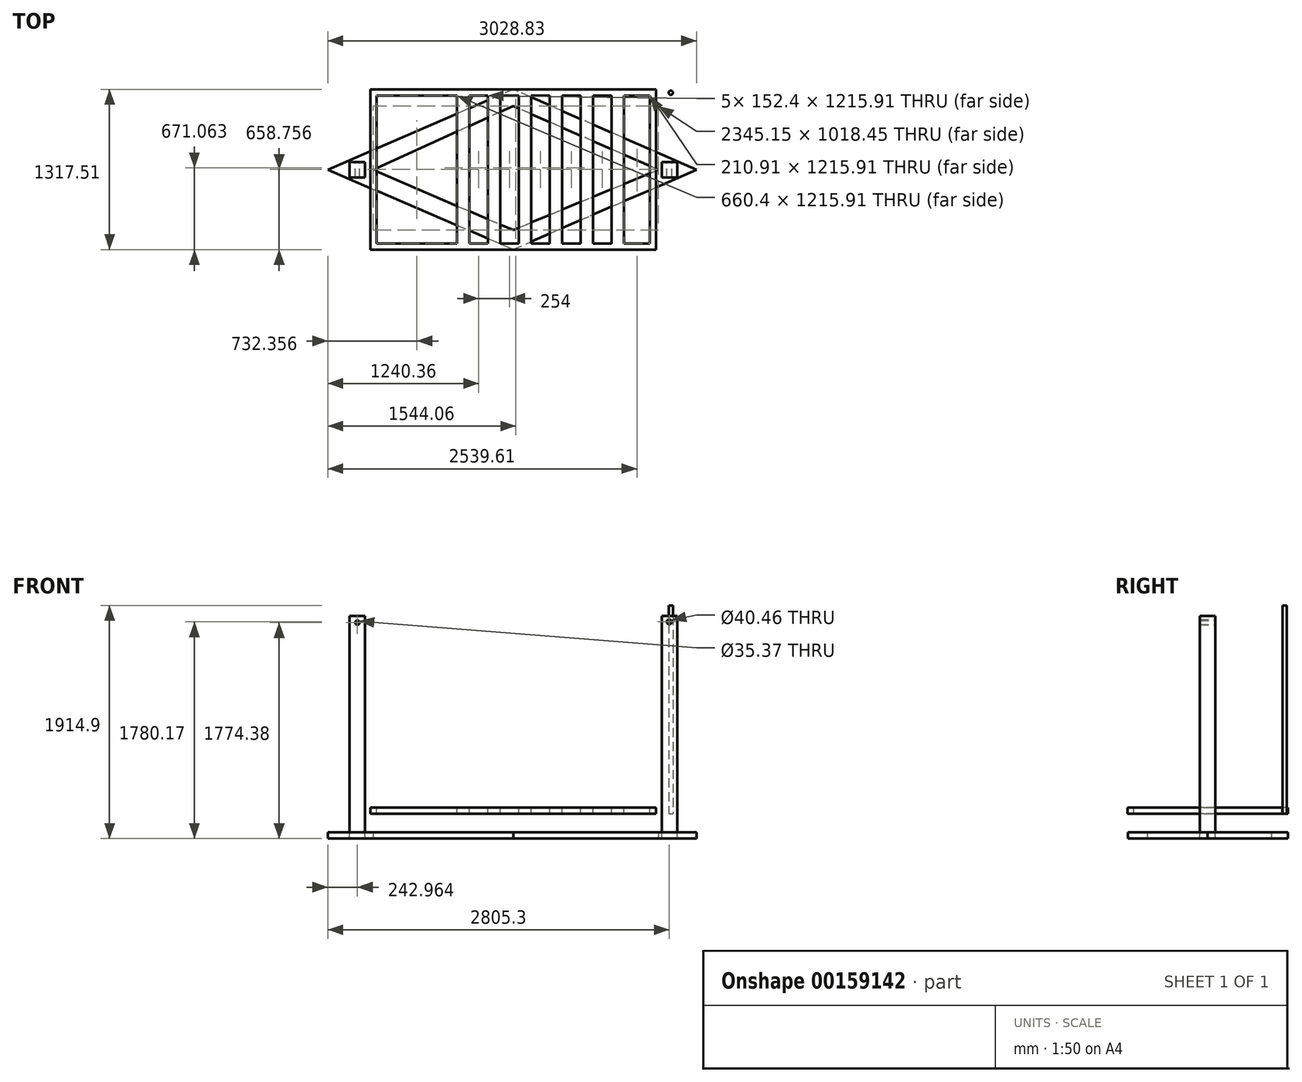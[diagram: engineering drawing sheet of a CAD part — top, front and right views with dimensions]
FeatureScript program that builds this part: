
annotation { "Feature Type Name" : "Feature", "Feature Type Description" : "" }
export const myFeature = defineFeature(function(context is Context, id is Id, definition is map)
    precondition{}
    {
        {
            var Q0;
            Q0=qCreatedBy(makeId("Front.planeOp"),FACE);
            var sketch = newSketch(context, id + "F0", { "sketchPlane" : qUnion([Q0])});
            skLineSegment(sketch, "E0", {"start": v(0, 0) * mm, "end": v(-1219.2, 0) * mm});
            skLineSegment(sketch, "E1", {"start": v(0, 0) * mm, "end": v(1219.2, 0) * mm});
            skLineSegment(sketch, "E2.bottom", {"start": v(-1219.2, 0) * mm, "end": v(-1346.2, 0) * mm});
            skLineSegment(sketch, "E2.top", {"start": v(-1219.2, 1828.8) * mm, "end": v(-1346.2, 1828.8) * mm});
            skLineSegment(sketch, "E2.left", {"start": v(-1219.2, 0) * mm, "end": v(-1219.2, 1828.8) * mm});
            skLineSegment(sketch, "E2.right", {"start": v(-1346.2, 0) * mm, "end": v(-1346.2, 1828.8) * mm});
            skLineSegment(sketch, "E3.bottom", {"start": v(1219.2, 0) * mm, "end": v(1346.2, 0) * mm});
            skLineSegment(sketch, "E3.top", {"start": v(1219.2, 1828.8) * mm, "end": v(1346.2, 1828.8) * mm});
            skLineSegment(sketch, "E3.left", {"start": v(1219.2, 0) * mm, "end": v(1219.2, 1828.8) * mm});
            skLineSegment(sketch, "E3.right", {"start": v(1346.2, 0) * mm, "end": v(1346.2, 1828.8) * mm});
            skSolve(sketch);
        }
        {
            var Q0;
            Q0=makeQuery(id+"F0.imprint","IMPRINT",FACE,{"disambiguationData":[TD([[makeQuery(id+"F0.imprint","IMPRINT",EDGE,{"derivedFrom":sQuery(id+"F0.wireOp",EDGE,"E2.bottom")}),-1.0]])]});
            var Q1;
            Q1=makeQuery(id+"F0.imprint","IMPRINT",FACE,{"disambiguationData":[TD([[makeQuery(id+"F0.imprint","IMPRINT",EDGE,{"derivedFrom":sQuery(id+"F0.wireOp",EDGE,"E3.bottom")}),1.0]])]});
            extrude(context, id + "F1", {"entities" : qUnion([Q0, Q1]), "depth" : 127 * mm, "symmetric" : true});
        }
        {
            var Q0;
            Q0=qCreatedBy(makeId("Top.planeOp"),FACE);
            var sketch = newSketch(context, id + "F2", { "sketchPlane" : qUnion([Q0])});
            skLineSegment(sketch, "E4.bottom", {"start": v(-1172.25, -656.01) * mm, "end": v(1172.25, -656.01) * mm});
            skLineSegment(sketch, "E4.top", {"start": v(-1172.25, 656.01) * mm, "end": v(1172.25, 656.01) * mm});
            skLineSegment(sketch, "E4.left", {"start": v(-1172.25, -656.01) * mm, "end": v(-1172.25, 656.01) * mm});
            skLineSegment(sketch, "E4.right", {"start": v(1172.25, -656.01) * mm, "end": v(1172.25, 656.01) * mm});
            skPoint(sketch, "E4.middle", {"position": v(0, 0) * mm});
            skSolve(sketch);
        }
        {
            var Q0;
            Q0 = qSketchRegion(id + "F2", true);
            extrude(context, id + "F3", {"entities" : qUnion([Q0]), "depth" : 76.2 * mm});
        }
        {
            var Q0;
            Q0=qCreatedBy(makeId("Front.planeOp"),FACE);
            var sketch = newSketch(context, id + "F4", { "sketchPlane" : qUnion([Q0])});
            skCircle(sketch, "E5", {"center": v(-1280.65, 1774.38) * mm, "radius": 17.68 * mm});
            skSolve(sketch);
        }
        {
            var Q0;
            Q0=makeQuery(id+"F4.imprint","IMPRINT",FACE,{"disambiguationData":[TD([[makeQuery(id+"F4.imprint","IMPRINT",EDGE,{"derivedFrom":sQuery(id+"F4.wireOp",EDGE,"E5")}),1.0]])]});
            extrude(context, id + "F5", {"entities" : qUnion([Q0]), "operationType" : NewBodyOperationType.REMOVE, "endBound" : BoundingType.THROUGH_ALL, "depth" : 147.7 * mm, "hasSecondDirection" : true, "secondDirectionOppositeDirection" : true, "secondDirectionDepth" : 166.4 * mm});
        }
        {
            var Q0;
            Q0=qCreatedBy(makeId("Front.planeOp"),FACE);
            var sketch = newSketch(context, id + "F6", { "sketchPlane" : qUnion([Q0])});
            skCircle(sketch, "E6", {"center": v(1281.68, 1780.17) * mm, "radius": 20.23 * mm});
            skSolve(sketch);
        }
        {
            var Q0;
            Q0 = qSketchRegion(id + "F6", true);
            extrude(context, id + "F7", {"entities" : qUnion([Q0]), "operationType" : NewBodyOperationType.REMOVE, "endBound" : BoundingType.UP_TO_NEXT, "depth" : 25.4 * mm, "hasSecondDirection" : true, "secondDirectionOppositeDirection" : true, "secondDirectionDepth" : 170.98 * mm});
        }
        {
            var Q0;
            Q0=qCreatedBy(makeId("Top.planeOp"),FACE);
            var sketch = newSketch(context, id + "F8", { "sketchPlane" : qUnion([Q0])});
            skLineSegment(sketch, "E7", {"start": v(-1523.6, 0) * mm, "end": v(0, -653.51) * mm});
            skLineSegment(sketch, "E8", {"start": v(0, -653.51) * mm, "end": v(1505.22, 0) * mm});
            skLineSegment(sketch, "E9", {"start": v(1505.22, 0) * mm, "end": v(0, 661.47) * mm});
            skLineSegment(sketch, "E10", {"start": v(0, 661.47) * mm, "end": v(-1523.6, 0) * mm});
            skLineSegment(sketch, "E11", {"start": v(-1152.12, 0) * mm, "end": v(0, -494.17) * mm});
            skLineSegment(sketch, "E12", {"start": v(0, -494.17) * mm, "end": v(1193.02, 0) * mm});
            skLineSegment(sketch, "E13", {"start": v(1193.02, 0) * mm, "end": v(0, 524.28) * mm});
            skLineSegment(sketch, "E14", {"start": v(0, 524.28) * mm, "end": v(-1152.12, 0) * mm});
            skSolve(sketch);
        }
        {
            var Q0;
            Q0=makeQuery(id+"F8.imprint","IMPRINT",FACE,{"disambiguationData":[TD([[makeQuery(id+"F8.imprint","IMPRINT",EDGE,{"derivedFrom":sQuery(id+"F8.wireOp",EDGE,"E7")}),1.0]])]});
            extrude(context, id + "F9", {"entities" : qUnion([Q0]), "depth" : 50.8 * mm});
        }
        {
            var Q0;
            Q0=makeQuery(id+"F3.opExtrude","SWEPT_FACE",FACE,{"disambiguationData":[OSD([sQuery(id+"F2.wireOp",EDGE,"E4.bottom")])]});
            var sketch = newSketch(context, id + "F10", { "sketchPlane" : qUnion([Q0])});
            skLineSegment(sketch, "E15.bottom", {"start": v(-1172.25, 389.27) * mm, "end": v(1172.25, 389.27) * mm});
            skLineSegment(sketch, "E15.top", {"start": v(-1172.25, 254) * mm, "end": v(1172.25, 254) * mm});
            skLineSegment(sketch, "E15.left", {"start": v(-1172.25, 389.27) * mm, "end": v(-1172.25, 254) * mm});
            skLineSegment(sketch, "E15.right", {"start": v(1172.25, 389.27) * mm, "end": v(1172.25, 254) * mm});
            skSolve(sketch);
        }
        {
            var Q0;
            Q0=makeQuery(id+"F10.imprint","IMPRINT",FACE,{"disambiguationData":[TD([[makeQuery(id+"F10.imprint","IMPRINT",EDGE,{"derivedFrom":sQuery(id+"F10.wireOp",EDGE,"E15.bottom")}),-1.0]])]});
            extrude(context, id + "F11", {"entities" : qUnion([Q0]), "oppositeDirection" : true, "depth" : 1320.8 * mm});
        }
        {
            var Q0;
            Q0=makeQuery(id+"F3.opExtrude","SWEPT_BODY",BODY,{"disambiguationData":[OSD([sQuery(id+"F2.wireOp",EDGE,"E4.bottom"),sQuery(id+"F2.wireOp",EDGE,"E4.top"),sQuery(id+"F2.wireOp",EDGE,"E4.left"),sQuery(id+"F2.wireOp",EDGE,"E4.right")])]});
            deleteBodies(context, id + "F12", {"entities" : qUnion([Q0])});
        }
        {
            var Q0;
            Q0=makeQuery(id+"F11.opExtrude","SWEPT_FACE",FACE,{"disambiguationData":[OSD([sQuery(id+"F10.wireOp",EDGE,"E15.top")])]});
            var sketch = newSketch(context, id + "F13", { "sketchPlane" : qUnion([Q0])});
            skLineSegment(sketch, "E16.bottom", {"start": v(-1172.25, 656.01) * mm, "end": v(1172.25, 656.01) * mm});
            skLineSegment(sketch, "E16.top", {"start": v(-1172.25, -661.5) * mm, "end": v(1172.25, -661.5) * mm});
            skLineSegment(sketch, "E16.left", {"start": v(-1172.25, 656.01) * mm, "end": v(-1172.25, -661.5) * mm});
            skLineSegment(sketch, "E16.right", {"start": v(1172.25, 656.01) * mm, "end": v(1172.25, -661.5) * mm});
            skLineSegment(sketch, "E17.0", {"start": v(-1121.45, 605.21) * mm, "end": v(1121.45, 605.21) * mm});
            skLineSegment(sketch, "E17.1", {"start": v(-1121.45, 605.21) * mm, "end": v(-1121.45, -610.7) * mm});
            skLineSegment(sketch, "E17.2", {"start": v(-1121.45, -610.7) * mm, "end": v(1121.45, -610.7) * mm});
            skLineSegment(sketch, "E17.3", {"start": v(1121.45, 605.21) * mm, "end": v(1121.45, -610.7) * mm});
            skLineSegment(sketch, "E18.bottom", {"start": v(-969.05, 605.21) * mm, "end": v(-867.45, 605.21) * mm});
            skLineSegment(sketch, "E18.top", {"start": v(-969.05, -610.7) * mm, "end": v(-867.45, -610.7) * mm});
            skLineSegment(sketch, "E18.left", {"start": v(-969.05, 605.21) * mm, "end": v(-969.05, -610.7) * mm});
            skLineSegment(sketch, "E18.right", {"start": v(-867.45, 605.21) * mm, "end": v(-867.45, -610.7) * mm});
            skLineSegment(sketch, "E19.bottom", {"start": v(-715.05, 605.21) * mm, "end": v(-613.45, 605.21) * mm});
            skLineSegment(sketch, "E19.top", {"start": v(-715.05, -610.7) * mm, "end": v(-613.45, -610.7) * mm});
            skLineSegment(sketch, "E19.left", {"start": v(-715.05, 605.21) * mm, "end": v(-715.05, -610.7) * mm});
            skLineSegment(sketch, "E19.right", {"start": v(-613.45, 605.21) * mm, "end": v(-613.45, -610.7) * mm});
            skLineSegment(sketch, "E20", {"start": v(-461.05, 605.21) * mm, "end": v(-461.05, -610.7) * mm});
            skLineSegment(sketch, "E21", {"start": v(-359.45, 605.21) * mm, "end": v(-359.45, -610.7) * mm});
            skLineSegment(sketch, "E22", {"start": v(-207.05, 605.21) * mm, "end": v(-207.05, -610.7) * mm});
            skPoint(sketch, "E22.endSnap0", {"position": v(0, -610.7) * mm});
            skLineSegment(sketch, "E23", {"start": v(-105.45, 605.21) * mm, "end": v(-105.45, -610.7) * mm});
            skLineSegment(sketch, "E24", {"start": v(46.95, 605.21) * mm, "end": v(46.95, -610.7) * mm});
            skLineSegment(sketch, "E25", {"start": v(148.55, 605.21) * mm, "end": v(148.55, -610.7) * mm});
            skLineSegment(sketch, "E26", {"start": v(300.95, 605.21) * mm, "end": v(300.95, -610.7) * mm});
            skLineSegment(sketch, "E27", {"start": v(402.55, 605.21) * mm, "end": v(402.55, -610.7) * mm});
            skLineSegment(sketch, "E28", {"start": v(554.95, 605.21) * mm, "end": v(554.95, -610.7) * mm});
            skLineSegment(sketch, "E29", {"start": v(656.55, 605.21) * mm, "end": v(656.55, -610.7) * mm});
            skLineSegment(sketch, "E30", {"start": v(808.95, 605.21) * mm, "end": v(808.95, -610.7) * mm});
            skLineSegment(sketch, "E31", {"start": v(910.55, 605.21) * mm, "end": v(910.55, -610.7) * mm});
            skSolve(sketch);
        }
        {
            var Q0;
            Q0=makeQuery(id+"F13.imprint","IMPRINT",FACE,{"disambiguationData":[TD([[makeQuery(id+"F13.imprint","IMPRINT",EDGE,{"derivedFrom":sQuery(id+"F13.wireOp",EDGE,"E16.bottom")}),-1.0]])]});
            var Q1;
            {var subQ0=sQuery(id+"F13.wireOp",EDGE,"E28");Q1=makeQuery(id+"F13.imprint","IMPRINT",FACE,{"disambiguationData":[TD([[makeQuery(id+"F13.imprint","IMPRINT",EDGE,{"derivedFrom":subQ0}),1.0]])]});}
            var Q2;
            {var subQ0=sQuery(id+"F13.wireOp",EDGE,"E22");Q2=makeQuery(id+"F13.imprint","IMPRINT",FACE,{"disambiguationData":[TD([[makeQuery(id+"F13.imprint","IMPRINT",EDGE,{"derivedFrom":subQ0}),1.0]])]});}
            var Q3;
            Q3=makeQuery(id+"F13.imprint","IMPRINT",FACE,{"disambiguationData":[TD([[makeQuery(id+"F13.imprint","IMPRINT",EDGE,{"derivedFrom":sQuery(id+"F13.wireOp",EDGE,"E19.bottom")}),-1.0]])]});
            var Q4;
            {var subQ0=sQuery(id+"F13.wireOp",EDGE,"E24");Q4=makeQuery(id+"F13.imprint","IMPRINT",FACE,{"disambiguationData":[TD([[makeQuery(id+"F13.imprint","IMPRINT",EDGE,{"derivedFrom":subQ0}),1.0]])]});}
            var Q5;
            {var subQ0=sQuery(id+"F13.wireOp",EDGE,"E20");Q5=makeQuery(id+"F13.imprint","IMPRINT",FACE,{"disambiguationData":[TD([[makeQuery(id+"F13.imprint","IMPRINT",EDGE,{"derivedFrom":subQ0}),1.0]])]});}
            var Q6;
            {var subQ0=sQuery(id+"F13.wireOp",EDGE,"E30");Q6=makeQuery(id+"F13.imprint","IMPRINT",FACE,{"disambiguationData":[TD([[makeQuery(id+"F13.imprint","IMPRINT",EDGE,{"derivedFrom":subQ0}),1.0]])]});}
            var Q7;
            Q7=makeQuery(id+"F13.imprint","IMPRINT",FACE,{"disambiguationData":[TD([[makeQuery(id+"F13.imprint","IMPRINT",EDGE,{"derivedFrom":sQuery(id+"F13.wireOp",EDGE,"E18.bottom")}),-1.0]])]});
            var Q8;
            {var subQ0=sQuery(id+"F13.wireOp",EDGE,"E26");Q8=makeQuery(id+"F13.imprint","IMPRINT",FACE,{"disambiguationData":[TD([[makeQuery(id+"F13.imprint","IMPRINT",EDGE,{"derivedFrom":subQ0}),1.0]])]});}
            extrude(context, id + "F14", {"entities" : qUnion([Q0, Q1, Q2, Q3, Q4, Q5, Q6, Q7, Q8]), "operationType" : NewBodyOperationType.ADD, "depth" : 50.8 * mm});
        }
        {
            var Q0;
            Q0=makeQuery(id+"F11.opExtrude","SWEPT_BODY",BODY,{"disambiguationData":[OSD([sQuery(id+"F10.wireOp",EDGE,"E15.bottom"),sQuery(id+"F10.wireOp",EDGE,"E15.top"),sQuery(id+"F10.wireOp",EDGE,"E15.left"),sQuery(id+"F10.wireOp",EDGE,"E15.right")])]});
            deleteBodies(context, id + "F15", {"entities" : qUnion([Q0])});
        }
        {
            var Q0;
            Q0=makeQuery(id+"F13.imprint","IMPRINT",FACE,{"disambiguationData":[TD([[makeQuery(id+"F13.imprint","IMPRINT",EDGE,{"derivedFrom":sQuery(id+"F13.wireOp",EDGE,"E16.bottom")}),-1.0]])]});
            var Q1;
            Q1=makeQuery(id+"F13.imprint","IMPRINT",FACE,{"disambiguationData":[TD([[makeQuery(id+"F13.imprint","IMPRINT",EDGE,{"derivedFrom":sQuery(id+"F13.wireOp",EDGE,"E18.bottom")}),-1.0]])]});
            var Q2;
            Q2=makeQuery(id+"F13.imprint","IMPRINT",FACE,{"disambiguationData":[TD([[makeQuery(id+"F13.imprint","IMPRINT",EDGE,{"derivedFrom":sQuery(id+"F13.wireOp",EDGE,"E19.bottom")}),-1.0]])]});
            var Q3;
            {var subQ0=sQuery(id+"F13.wireOp",EDGE,"E20");Q3=makeQuery(id+"F13.imprint","IMPRINT",FACE,{"disambiguationData":[TD([[makeQuery(id+"F13.imprint","IMPRINT",EDGE,{"derivedFrom":subQ0}),1.0]])]});}
            var Q4;
            {var subQ0=sQuery(id+"F13.wireOp",EDGE,"E22");Q4=makeQuery(id+"F13.imprint","IMPRINT",FACE,{"disambiguationData":[TD([[makeQuery(id+"F13.imprint","IMPRINT",EDGE,{"derivedFrom":subQ0}),1.0]])]});}
            var Q5;
            {var subQ0=sQuery(id+"F13.wireOp",EDGE,"E24");Q5=makeQuery(id+"F13.imprint","IMPRINT",FACE,{"disambiguationData":[TD([[makeQuery(id+"F13.imprint","IMPRINT",EDGE,{"derivedFrom":subQ0}),1.0]])]});}
            var Q6;
            {var subQ0=sQuery(id+"F13.wireOp",EDGE,"E26");Q6=makeQuery(id+"F13.imprint","IMPRINT",FACE,{"disambiguationData":[TD([[makeQuery(id+"F13.imprint","IMPRINT",EDGE,{"derivedFrom":subQ0}),1.0]])]});}
            var Q7;
            {var subQ0=sQuery(id+"F13.wireOp",EDGE,"E28");Q7=makeQuery(id+"F13.imprint","IMPRINT",FACE,{"disambiguationData":[TD([[makeQuery(id+"F13.imprint","IMPRINT",EDGE,{"derivedFrom":subQ0}),1.0]])]});}
            var Q8;
            {var subQ0=sQuery(id+"F13.wireOp",EDGE,"E30");Q8=makeQuery(id+"F13.imprint","IMPRINT",FACE,{"disambiguationData":[TD([[makeQuery(id+"F13.imprint","IMPRINT",EDGE,{"derivedFrom":subQ0}),1.0]])]});}
            extrude(context, id + "F16", {"entities" : qUnion([Q0, Q1, Q2, Q3, Q4, Q5, Q6, Q7, Q8]), "depth" : 50.8 * mm});
        }
        {
            var Q0;
            Q0=makeQuery(id+"F16.opExtrude","SWEPT_FACE",FACE,{"disambiguationData":[OSD([sQuery(id+"F13.wireOp",EDGE,"E16.bottom")])]});
            cPlane(context, id + "F17", {"entities" : qUnion([Q0]), "cplaneType" : CPlaneType.OFFSET, "offset" : 25.4 * mm, "width" : 152.4 * mm, "height" : 152.4 * mm});
        }
        {
            var Q0;
            Q0=qCreatedBy(makeId("Front.planeOp"),FACE);
            var sketch = newSketch(context, id + "F18", { "sketchPlane" : qUnion([Q0])});
            skLineSegment(sketch, "E32", {"start": v(0, 0) * mm, "end": v(501.44, 1836.12) * mm});
            skSolve(sketch);
        }
        {
            var Q0;
            Q0=qCreatedBy(makeId("Top.planeOp"),FACE);
            var sketch = newSketch(context, id + "F19", { "sketchPlane" : qUnion([Q0])});
            skCircle(sketch, "E33", {"center": v(0, 0) * mm, "radius": 16.95 * mm});
            skSolve(sketch);
        }
        {
            var Q0;
            Q0=makeQuery(id+"F16.opExtrude","CAP_EDGE",EDGE,{"disambiguationData":[OSD([sQuery(id+"F13.wireOp",EDGE,"E16.right")])],"isStart":false});
            cPlane(context, id + "F20", {"entities" : qUnion([Q0]), "cplaneType" : CPlaneType.LINE_ANGLE, "offset" : 25.4 * mm, "angle" : 0 * degree, "width" : 152.4 * mm, "height" : 152.4 * mm});
        }
        {
            var Q0;
            Q0=qCreatedBy(id+"F20.planeOp",FACE);
            var sketch = newSketch(context, id + "F21", { "sketchPlane" : qUnion([Q0])});
            skCircle(sketch, "E34", {"center": v(1293.8, -633.39) * mm, "radius": 17.52 * mm});
            skSolve(sketch);
        }
        {
            var Q0;
            Q0 = qSketchRegion(id + "F21", true);
            extrude(context, id + "F22", {"entities" : qUnion([Q0]), "oppositeDirection" : true, "depth" : 1711.7 * mm});
        }
    });
